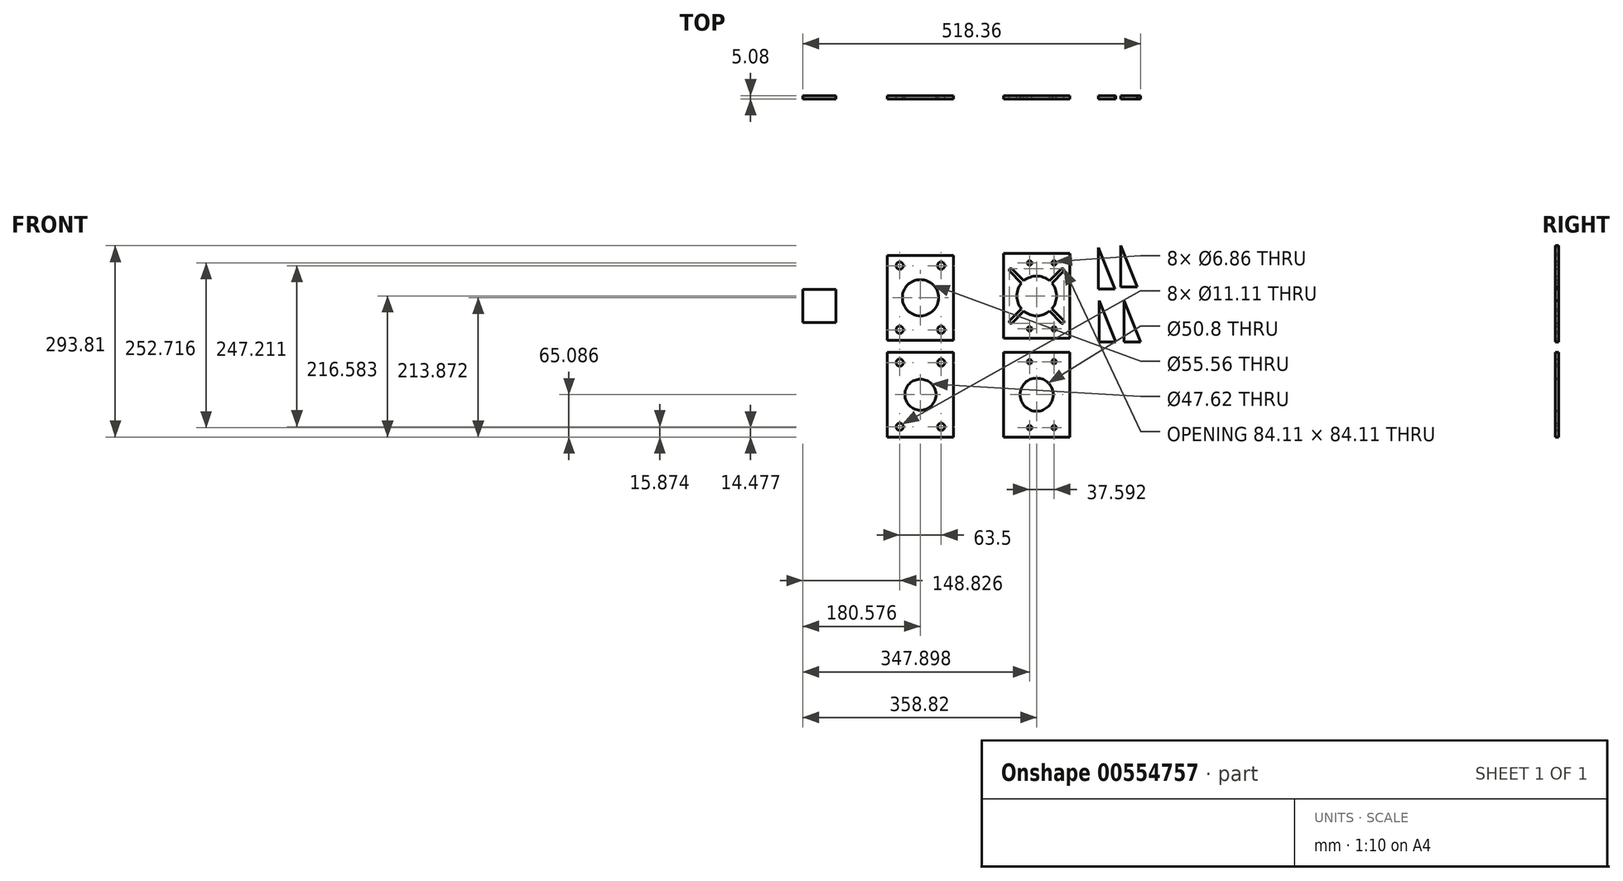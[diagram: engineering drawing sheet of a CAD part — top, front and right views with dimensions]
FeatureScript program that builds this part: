
annotation { "Feature Type Name" : "Feature", "Feature Type Description" : "" }
export const myFeature = defineFeature(function(context is Context, id is Id, definition is map)
    precondition{}
    {
        {
            var Q0;
            Q0=qCreatedBy(makeId("Front.planeOp"),FACE);
            var sketch = newSketch(context, id + "F0", { "sketchPlane" : qUnion([Q0])});
            skLineSegment(sketch, "E0.bottom", {"start": v(-108.11, 130.09) * mm, "end": v(-6.51, 130.09) * mm});
            skLineSegment(sketch, "E0.top", {"start": v(-108.11, -0.09) * mm, "end": v(-6.51, -0.09) * mm});
            skLineSegment(sketch, "E0.left", {"start": v(-108.11, 130.09) * mm, "end": v(-108.11, -0.09) * mm});
            skLineSegment(sketch, "E0.right", {"start": v(-6.51, 130.09) * mm, "end": v(-6.51, -0.09) * mm});
            skCircle(sketch, "E1", {"center": v(-57.31, 65) * mm, "radius": 27.78 * mm});
            skPoint(sketch, "E1.centerSnap0", {"position": v(-108.11, 65) * mm});
            skPoint(sketch, "E1.centerSnap1", {"position": v(-57.31, 130.09) * mm});
            skCircle(sketch, "E2", {"center": v(-89.06, 114.21) * mm, "radius": 5.56 * mm});
            skCircle(sketch, "E3", {"center": v(-25.56, 114.21) * mm, "radius": 5.56 * mm});
            skCircle(sketch, "E4", {"center": v(-25.56, 15.79) * mm, "radius": 5.56 * mm});
            skCircle(sketch, "E5", {"center": v(-89.06, 15.79) * mm, "radius": 5.56 * mm});
            skLineSegment(sketch, "E6.bottom", {"start": v(-108.11, -18.7) * mm, "end": v(-6.51, -18.7) * mm});
            skLineSegment(sketch, "E6.top", {"start": v(-108.11, -148.87) * mm, "end": v(-6.51, -148.87) * mm});
            skLineSegment(sketch, "E6.left", {"start": v(-108.11, -18.7) * mm, "end": v(-108.11, -148.87) * mm});
            skLineSegment(sketch, "E6.right", {"start": v(-6.51, -18.7) * mm, "end": v(-6.51, -148.87) * mm});
            skCircle(sketch, "E7", {"center": v(-57.31, -83.78) * mm, "radius": 23.81 * mm});
            skPoint(sketch, "E7.centerSnap0", {"position": v(-108.11, -83.78) * mm});
            skPoint(sketch, "E7.centerSnap1", {"position": v(-57.31, -18.7) * mm});
            skCircle(sketch, "E8", {"center": v(-89.06, -34.57) * mm, "radius": 5.56 * mm});
            skCircle(sketch, "E9", {"center": v(-25.56, -34.57) * mm, "radius": 5.56 * mm});
            skCircle(sketch, "E10", {"center": v(-25.56, -133) * mm, "radius": 5.56 * mm});
            skCircle(sketch, "E11", {"center": v(-89.06, -133) * mm, "radius": 5.56 * mm});
            skLineSegment(sketch, "E12.bottom", {"start": v(70.13, 132.8) * mm, "end": v(171.73, 132.8) * mm});
            skLineSegment(sketch, "E12.top", {"start": v(70.13, 2.63) * mm, "end": v(171.73, 2.63) * mm});
            skLineSegment(sketch, "E12.left", {"start": v(70.13, 132.8) * mm, "end": v(70.13, 2.63) * mm});
            skLineSegment(sketch, "E12.right", {"start": v(171.73, 132.8) * mm, "end": v(171.73, 2.63) * mm});
            skCircle(sketch, "E13", {"center": v(120.93, 67.71) * mm, "radius": 30.48 * mm});
            skPoint(sketch, "E13.centerSnap0", {"position": v(70.13, 67.71) * mm});
            skPoint(sketch, "E13.centerSnap1", {"position": v(120.93, 132.8) * mm});
            skCircle(sketch, "E14", {"center": v(110, 118.32) * mm, "radius": 3.43 * mm});
            skCircle(sketch, "E15", {"center": v(147.6, 118.32) * mm, "radius": 3.43 * mm});
            skCircle(sketch, "E16", {"center": v(147.6, 17.1) * mm, "radius": 3.43 * mm});
            skCircle(sketch, "E17", {"center": v(110, 17.1) * mm, "radius": 3.43 * mm});
            skLineSegment(sketch, "E18.bottom", {"start": v(70.13, -18.7) * mm, "end": v(171.73, -18.7) * mm});
            skLineSegment(sketch, "E18.top", {"start": v(70.13, -148.87) * mm, "end": v(171.73, -148.87) * mm});
            skLineSegment(sketch, "E18.left", {"start": v(70.13, -18.7) * mm, "end": v(70.13, -148.87) * mm});
            skLineSegment(sketch, "E18.right", {"start": v(171.73, -18.7) * mm, "end": v(171.73, -148.87) * mm});
            skCircle(sketch, "E19", {"center": v(120.93, -83.78) * mm, "radius": 25.4 * mm});
            skPoint(sketch, "E19.centerSnap0", {"position": v(70.13, -83.78) * mm});
            skPoint(sketch, "E19.centerSnap1", {"position": v(120.93, -18.7) * mm});
            skCircle(sketch, "E20", {"center": v(110, -33.17) * mm, "radius": 3.43 * mm});
            skCircle(sketch, "E21", {"center": v(147.6, -33.17) * mm, "radius": 3.43 * mm});
            skCircle(sketch, "E22", {"center": v(147.6, -134.4) * mm, "radius": 3.43 * mm});
            skCircle(sketch, "E23", {"center": v(110, -134.4) * mm, "radius": 3.43 * mm});
            skLineSegment(sketch, "E24", {"start": v(215.4, 141.76) * mm, "end": v(215.4, 78.26) * mm});
            skLineSegment(sketch, "E25", {"start": v(215.4, 78.26) * mm, "end": v(240.8, 78.26) * mm});
            skLineSegment(sketch, "E26", {"start": v(240.8, 78.26) * mm, "end": v(215.4, 141.76) * mm});
            skLineSegment(sketch, "E27", {"start": v(249.92, 144.94) * mm, "end": v(249.92, 81.44) * mm});
            skLineSegment(sketch, "E28", {"start": v(249.92, 81.44) * mm, "end": v(275.32, 81.44) * mm});
            skLineSegment(sketch, "E29", {"start": v(275.32, 81.44) * mm, "end": v(249.92, 144.94) * mm});
            skLineSegment(sketch, "E30", {"start": v(216.8, 60.3) * mm, "end": v(216.8, -3.2) * mm});
            skLineSegment(sketch, "E31", {"start": v(216.8, -3.2) * mm, "end": v(242.2, -3.2) * mm});
            skLineSegment(sketch, "E32", {"start": v(242.2, -3.2) * mm, "end": v(216.8, 60.3) * mm});
            skLineSegment(sketch, "E33", {"start": v(255.07, 60.3) * mm, "end": v(255.07, -3.2) * mm});
            skLineSegment(sketch, "E34", {"start": v(255.07, -3.2) * mm, "end": v(280.47, -3.2) * mm});
            skLineSegment(sketch, "E35", {"start": v(280.47, -3.2) * mm, "end": v(255.07, 60.3) * mm});
            skLineSegment(sketch, "E36", {"start": v(160.44, 107.23) * mm, "end": v(81.42, 28.2) * mm, "construction": true});
            skLineSegment(sketch, "E37", {"start": v(81.42, 107.23) * mm, "end": v(160.44, 28.2) * mm, "construction": true});
            skLineSegment(sketch, "E38", {"start": v(120.93, 132.8) * mm, "end": v(120.93, 2.63) * mm, "construction": true});
            skLineSegment(sketch, "E39", {"start": v(70.13, 67.71) * mm, "end": v(171.73, 67.71) * mm, "construction": true});
            skArc(sketch, "E40.0.startCap", {"start": v(79.62, 105.43) * mm, "mid": v(79.62, 109.02) * mm, "end": v(83.21, 109.02) * mm});
            skArc(sketch, "E40.0.endCap", {"start": v(162.24, 30) * mm, "mid": v(162.24, 26.4) * mm, "end": v(158.65, 26.4) * mm});
            skLineSegment(sketch, "E40.0.left", {"start": v(83.21, 109.02) * mm, "end": v(162.24, 30) * mm});
            skLineSegment(sketch, "E40.0.right", {"start": v(79.62, 105.43) * mm, "end": v(158.65, 26.4) * mm});
            skArc(sketch, "E40.1.startCap", {"start": v(158.65, 109.02) * mm, "mid": v(162.24, 109.02) * mm, "end": v(162.24, 105.43) * mm});
            skArc(sketch, "E40.1.endCap", {"start": v(83.21, 26.4) * mm, "mid": v(79.62, 26.4) * mm, "end": v(79.62, 30) * mm});
            skLineSegment(sketch, "E40.1.left", {"start": v(162.24, 105.43) * mm, "end": v(83.21, 26.4) * mm});
            skLineSegment(sketch, "E40.1.right", {"start": v(158.65, 109.02) * mm, "end": v(79.62, 30) * mm});
            skLineSegment(sketch, "E41", {"start": v(79.62, 105.43) * mm, "end": v(83.21, 109.02) * mm});
            skLineSegment(sketch, "E42", {"start": v(158.65, 109.02) * mm, "end": v(162.24, 105.43) * mm});
            skLineSegment(sketch, "E43", {"start": v(162.24, 30) * mm, "end": v(158.65, 26.4) * mm});
            skLineSegment(sketch, "E44", {"start": v(83.21, 26.4) * mm, "end": v(79.62, 30) * mm});
            skLineSegment(sketch, "E45.bottom", {"start": v(-237.89, 77.88) * mm, "end": v(-187.09, 77.88) * mm});
            skLineSegment(sketch, "E45.top", {"start": v(-237.89, 27.08) * mm, "end": v(-187.09, 27.08) * mm});
            skLineSegment(sketch, "E45.left", {"start": v(-237.89, 77.88) * mm, "end": v(-237.89, 27.08) * mm});
            skLineSegment(sketch, "E45.right", {"start": v(-187.09, 77.88) * mm, "end": v(-187.09, 27.08) * mm});
            skSolve(sketch);
        }
        {
            var Q0;
            Q0=makeQuery(id+"F0.imprint","IMPRINT",FACE,{"disambiguationData":[TD([[makeQuery(id+"F0.imprint","IMPRINT",EDGE,{"derivedFrom":sQuery(id+"F0.wireOp",EDGE,"E0.bottom")}),-1.0]])]});
            var Q1;
            Q1=makeQuery(id+"F0.imprint","IMPRINT",FACE,{"disambiguationData":[TD([[makeQuery(id+"F0.imprint","IMPRINT",EDGE,{"derivedFrom":sQuery(id+"F0.wireOp",EDGE,"E12.bottom")}),-1.0]])]});
            var Q2;
            Q2=makeQuery(id+"F0.imprint","IMPRINT",FACE,{"disambiguationData":[TD([[makeQuery(id+"F0.imprint","IMPRINT",EDGE,{"derivedFrom":sQuery(id+"F0.wireOp",EDGE,"E18.bottom")}),-1.0]])]});
            var Q3;
            Q3=makeQuery(id+"F0.imprint","IMPRINT",FACE,{"disambiguationData":[TD([[makeQuery(id+"F0.imprint","IMPRINT",EDGE,{"derivedFrom":sQuery(id+"F0.wireOp",EDGE,"E6.bottom")}),-1.0]])]});
            var Q4;
            Q4=makeQuery(id+"F0.imprint","IMPRINT",FACE,{"disambiguationData":[TD([[makeQuery(id+"F0.imprint","IMPRINT",EDGE,{"derivedFrom":sQuery(id+"F0.wireOp",EDGE,"E24")}),1.0]])]});
            var Q5;
            Q5=makeQuery(id+"F0.imprint","IMPRINT",FACE,{"disambiguationData":[TD([[makeQuery(id+"F0.imprint","IMPRINT",EDGE,{"derivedFrom":sQuery(id+"F0.wireOp",EDGE,"E27")}),1.0]])]});
            var Q6;
            Q6=makeQuery(id+"F0.imprint","IMPRINT",FACE,{"disambiguationData":[TD([[makeQuery(id+"F0.imprint","IMPRINT",EDGE,{"derivedFrom":sQuery(id+"F0.wireOp",EDGE,"E30")}),1.0]])]});
            var Q7;
            Q7=makeQuery(id+"F0.imprint","IMPRINT",FACE,{"disambiguationData":[TD([[makeQuery(id+"F0.imprint","IMPRINT",EDGE,{"derivedFrom":sQuery(id+"F0.wireOp",EDGE,"E33")}),1.0]])]});
            var Q8;
            Q8=makeQuery(id+"F0.imprint","IMPRINT",FACE,{"disambiguationData":[TD([[makeQuery(id+"F0.imprint","IMPRINT",EDGE,{"derivedFrom":sQuery(id+"F0.wireOp",EDGE,"E40.0.startCap")}),-1.0]])]});
            var Q9;
            Q9=makeQuery(id+"F0.imprint","IMPRINT",FACE,{"disambiguationData":[TD([[makeQuery(id+"F0.imprint","IMPRINT",EDGE,{"derivedFrom":sQuery(id+"F0.wireOp",EDGE,"E40.1.startCap")}),-1.0]])]});
            var Q10;
            Q10=makeQuery(id+"F0.imprint","IMPRINT",FACE,{"disambiguationData":[TD([[makeQuery(id+"F0.imprint","IMPRINT",EDGE,{"derivedFrom":sQuery(id+"F0.wireOp",EDGE,"E40.0.endCap")}),-1.0]])]});
            var Q11;
            Q11=makeQuery(id+"F0.imprint","IMPRINT",FACE,{"disambiguationData":[TD([[makeQuery(id+"F0.imprint","IMPRINT",EDGE,{"derivedFrom":sQuery(id+"F0.wireOp",EDGE,"E40.1.endCap")}),-1.0]])]});
            var Q12;
            Q12=makeQuery(id+"F0.imprint","IMPRINT",FACE,{"disambiguationData":[TD([[makeQuery(id+"F0.imprint","IMPRINT",EDGE,{"derivedFrom":sQuery(id+"F0.wireOp",EDGE,"E45.bottom")}),-1.0]])]});
            extrude(context, id + "F1", {"entities" : qUnion([Q0, Q1, Q2, Q3, Q4, Q5, Q6, Q7, Q8, Q9, Q10, Q11, Q12]), "depth" : 5.08 * mm, "offsetDistance" : 25.4 * mm});
        }
    });
